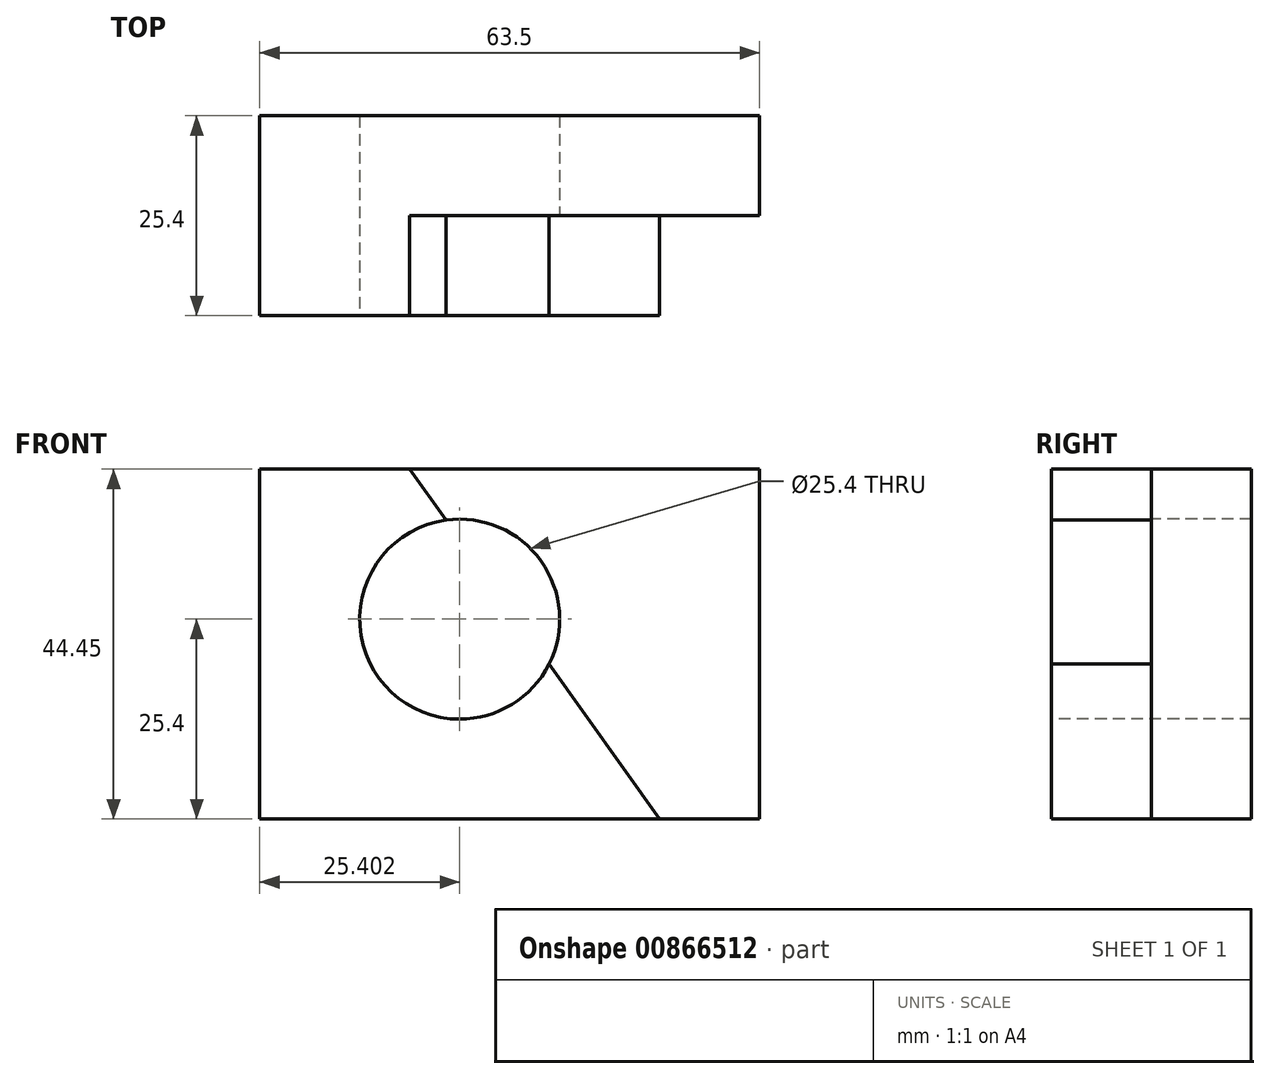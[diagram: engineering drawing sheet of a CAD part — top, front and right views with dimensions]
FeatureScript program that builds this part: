
annotation { "Feature Type Name" : "Feature", "Feature Type Description" : "" }
export const myFeature = defineFeature(function(context is Context, id is Id, definition is map)
    precondition{}
    {
        {
            var Q0;
            Q0=qCreatedBy(makeId("Top.planeOp"),FACE);
            var sketch = newSketch(context, id + "F0", { "sketchPlane" : qUnion([Q0])});
            skLineSegment(sketch, "E0.bottom", {"start": v(0.01, -0.54) * mm, "end": v(63.51, -0.54) * mm});
            skLineSegment(sketch, "E0.top", {"start": v(0.01, -25.94) * mm, "end": v(63.51, -25.94) * mm});
            skLineSegment(sketch, "E0.left", {"start": v(0.01, -0.54) * mm, "end": v(0.01, -25.94) * mm});
            skLineSegment(sketch, "E0.right", {"start": v(63.51, -0.54) * mm, "end": v(63.51, -25.94) * mm});
            skSolve(sketch);
        }
        {
            var Q0;
            Q0 = qSketchRegion(id + "F0", true);
            extrude(context, id + "F1", {"entities" : qUnion([Q0]), "depth" : 44.45 * mm, "offsetDistance" : 25.4 * mm});
        }
        {
            var Q0;
            Q0=makeQuery(id+"F1.opExtrude","SWEPT_FACE",FACE,{"disambiguationData":[OSD([sQuery(id+"F0.wireOp",EDGE,"E0.top")])]});
            var sketch = newSketch(context, id + "F2", { "sketchPlane" : qUnion([Q0])});
            skLineSegment(sketch, "E1", {"start": v(19.06, 44.45) * mm, "end": v(50.81, 0) * mm});
            skSolve(sketch);
        }
        {
            var Q0;
            Q0 = qSketchRegion(id + "F2", true);
            var Q1;
            {var subQ0=sQuery(id+"F2.wireOp",EDGE,"E1");Q1=makeQuery(id+"F2.imprint","IMPRINT",FACE,{"disambiguationData":[TD([[makeQuery(id+"F2.imprint","IMPRINT",EDGE,{"derivedFrom":subQ0}),1.0]])]});}
            extrude(context, id + "F3", {"entities" : qUnion([Q0, Q1]), "operationType" : NewBodyOperationType.REMOVE, "oppositeDirection" : true, "depth" : 12.7 * mm, "offsetDistance" : 25.4 * mm});
        }
        {
            var Q0;
            Q0=makeQuery(id+"F1.opExtrude","SWEPT_FACE",FACE,{"disambiguationData":[OSD([sQuery(id+"F0.wireOp",EDGE,"E0.top")])]});
            var sketch = newSketch(context, id + "F4", { "sketchPlane" : qUnion([Q0])});
            skCircle(sketch, "E2", {"center": v(25.41, 25.4) * mm, "radius": 12.7 * mm});
            skSolve(sketch);
        }
        {
            var Q0;
            Q0 = qSketchRegion(id + "F4", true);
            extrude(context, id + "F5", {"entities" : qUnion([Q0]), "operationType" : NewBodyOperationType.REMOVE, "oppositeDirection" : true, "depth" : 25.4 * mm, "offsetDistance" : 25.4 * mm});
        }
    });
